# Revit family: Hager-GOLF-Flush_mounted-IP40-With_Cover-With_DIN-NoHosted-PL-pl
name_source: partatom
category: Electrical Equipment
units: mm (PartAtom-declared; Revit-internal decimal feet)

## family parameters
Always vertical = Yes
Cut with Voids When Loaded = No
Maintain Annotation Orientation = No
Panel Configuration = Two Columns, Circuits Across
Part Type = Panelboard
Room Calculation Point = No
Round Connector Dimension = Use Diameter
Shared = No
Work Plane-Based = Yes

## types (25) — shared parameters
Code hager = ADD-EC000214_EU
Default Elevation = 1200 mm
EF000003 - Sposób montażu = Montaż podtynkowy
EF000007 - Kolor = Biały
EF000024 - Odporność na promieniowanie UV = No
EF000049 - Głębokość = 97 mm  [stored 0.318241 ft]
EF000116 - Numer RAL = 9010
EF000218 - Głębokość wbudowania = 72 mm  [stored 0.23622 ft]
EF001062 - Wykonanie zgodne z Dyrektywą Kompatybilności Elektromagnetycznej EMC = No
EF001088 - Możliwość rozbudowy = Yes
EF001134 - Szyna DIN = Yes
EF004462 - Rodzaj zamknięcia = Inne
EF005474 - Stopień ochrony (IP) = IP40
EF006306 - Z zamkiem = No
EF015941 - Drzwi przepuszczające sygnał = Yes
ETIM class code = EC000214
ETIM class name = Small distribution board
HG000001-Number of columns-pl = 1
HG000002-with door or cover-pl = Yes
HG000003-Range-pl = GOLF
HG000005-Thickness-pl = 2 mm  [stored 0.00656168 ft]
HG000006-Flush mounted-pl = Yes
HG000009-Double swing door-pl = No
HG000010-Asymmetric doors-pl = No
HG000011-Empty rows from bottom-pl = No
HG000012-Door swing angle-pl = 90.00°
HG000013-Door on the left-pl = No
HG000014-Door on the right-pl = Yes
HG000015-Clearance visibility-pl = Yes
HG000016-Door 3D visibility-pl = Yes
HG000017-Distance between poles-pl = 18 mm  [stored 0.0590551 ft]
HG000060-RAL-number = 9010
HG000099-Onfly Template ID-pl-PL = 507532
Manufacturer = Hager
Name BIM&CO = Electricity
Name hager = ADD_Enclosures_EC000214
Reference = Template-Enclosure_EU-EC000214
Uniformat = Low Tension Service & Dist.
Uniformat code = D501001
zero-valued in all types: EF001131 - Głębokość wewnętrzna, HG000007-Number of empty columns-pl, HG000008-Number of empty rows-pl

## per-type parameters (varying)
| type | BC_METADATA | EF000008 - Szerokość | EF000040 - Wysokość | EF000118 - Z płytą montażową | EF000266 - Liczba rzędów | EF000332 - Wysokość wbudowania | EF000846 - Szerokość wbudowania | EF002950 - Szerokość wyrażona liczbą modułów | EF006244 - Transparentna pokrywa/drzwi | EF009212 - Wykonanie/rodzaj pokrywy | EF015776 - Listwa zaciskowa uziemienia | EF015777 - Listwa zaciskowa przewodu neutralnego | HG000004-Manufacturer reference-pl | HGEF000266-Liczba rzędów | HGEF0002950-Szerokość wyrażona liczbą modułów |
| GOLF-Flush_mounted_W204_H225_D97_4_Modular_Spacing-VF104PD | {"ObjectGuid":"4110ddcc-8f0d-44ed-8822-63e9be82c284","ModelGuid":"366267af-4815-4317-b628-b26145f090ec","VariantGuid":"5908c0a0-e7f0-400e-9d29-8d09325588ac","Revision":"#12","VariantName":"GOLF-Flush_mounted_W204_H225_D97_4_Modular_Spacing-VF104PD"} | 204 mm | 225 mm  [stored 0.738189 ft] | No | 1 | 189 mm  [stored 0.620079 ft] | 170 mm  [stored 0.557743 ft] | 4 | No | Zamknięty | Yes | Yes | VF104PD | 1 | 4 |
| GOLF-Flush_mounted_W204_H225_D97_4_Modular_Spacing-VF104TD | {"ObjectGuid":"4110ddcc-8f0d-44ed-8822-63e9be82c284","ModelGuid":"366267af-4815-4317-b628-b26145f090ec","VariantGuid":"e0216446-62ca-4817-b7ef-b2e9ca912061","Revision":"#12","VariantName":"GOLF-Flush_mounted_W204_H225_D97_4_Modular_Spacing-VF104TD"} | 204 mm | 225 mm  [stored 0.738189 ft] | No | 1 | 189 mm  [stored 0.620079 ft] | 170 mm  [stored 0.557743 ft] | 4 | Yes | Zamknięty | Yes | Yes | VF104TD | 1 | 4 |
| GOLF-Flush_mounted_W275_H225_D97_8_Modular_Spacing-VF108PD | {"ObjectGuid":"4110ddcc-8f0d-44ed-8822-63e9be82c284","ModelGuid":"366267af-4815-4317-b628-b26145f090ec","VariantGuid":"b03ebf87-6662-491a-b6a8-509a16b323ed","Revision":"#12","VariantName":"GOLF-Flush_mounted_W275_H225_D97_8_Modular_Spacing-VF108PD"} | 275 mm | 225 mm  [stored 0.738189 ft] | No | 1 | 189 mm  [stored 0.620079 ft] | 242 mm  [stored 0.793963 ft] | 8 | No | Zamknięty | Yes | Yes | VF108PD | 1 | 8 |
| GOLF-Flush_mounted_W275_H225_D97_8_Modular_Spacing-VF108TD | {"ObjectGuid":"4110ddcc-8f0d-44ed-8822-63e9be82c284","ModelGuid":"366267af-4815-4317-b628-b26145f090ec","VariantGuid":"675cc267-a1fb-44dc-9656-e9b862e703bb","Revision":"#12","VariantName":"GOLF-Flush_mounted_W275_H225_D97_8_Modular_Spacing-VF108TD"} | 275 mm | 225 mm  [stored 0.738189 ft] | No | 1 | 189 mm  [stored 0.620079 ft] | 242 mm  [stored 0.793963 ft] | 8 | Yes | Zamknięty | Yes | Yes | VF108TD | 1 | 8 |
| GOLF-Flush_mounted_W352_H293_D97_12_Modular_Spacing-VF112PD | {"ObjectGuid":"4110ddcc-8f0d-44ed-8822-63e9be82c284","ModelGuid":"366267af-4815-4317-b628-b26145f090ec","VariantGuid":"7fc8be5a-4e42-4c11-bf83-f1857e61b970","Revision":"#12","VariantName":"GOLF-Flush_mounted_W352_H293_D97_12_Modular_Spacing-VF112PD"} | 352 mm  [stored 1.15486 ft] | 293 mm | No | 1 | 257 mm  [stored 0.843176 ft] | 318 mm  [stored 1.04331 ft] | 12 | No | Zamknięty | Yes | Yes | VF112PD | 1 | 12 |
| GOLF-Flush_mounted_W352_H293_D97_12_Modular_Spacing-VF112TD | {"ObjectGuid":"4110ddcc-8f0d-44ed-8822-63e9be82c284","ModelGuid":"366267af-4815-4317-b628-b26145f090ec","VariantGuid":"7087be8a-5bcc-4a63-bb2f-b231d84baee1","Revision":"#12","VariantName":"GOLF-Flush_mounted_W352_H293_D97_12_Modular_Spacing-VF112TD"} | 352 mm  [stored 1.15486 ft] | 293 mm | No | 1 | 257 mm  [stored 0.843176 ft] | 318 mm  [stored 1.04331 ft] | 12 | Yes | Zamknięty | Yes | Yes | VF112TD | 1 | 12 |
| GOLF-Flush_mounted_W460_H293_D97_18_Modular_Spacing-VF118PD | {"ObjectGuid":"4110ddcc-8f0d-44ed-8822-63e9be82c284","ModelGuid":"366267af-4815-4317-b628-b26145f090ec","VariantGuid":"b158a517-640d-4d6e-841f-1372ac4b0368","Revision":"#12","VariantName":"GOLF-Flush_mounted_W460_H293_D97_18_Modular_Spacing-VF118PD"} | 460 mm  [stored 1.50919 ft] | 293 mm | No | 1 | 257 mm  [stored 0.843176 ft] | 426 mm  [stored 1.39764 ft] | 18 | No | Zamknięty | Yes | Yes | VF118PD | 1 | 18 |
| GOLF-Flush_mounted_W460_H293_D97_18_Modular_Spacing-VF118TD | {"ObjectGuid":"4110ddcc-8f0d-44ed-8822-63e9be82c284","ModelGuid":"366267af-4815-4317-b628-b26145f090ec","VariantGuid":"ca84ee14-7eb6-47c0-83a6-df2615128fcd","Revision":"#12","VariantName":"GOLF-Flush_mounted_W460_H293_D97_18_Modular_Spacing-VF118TD"} | 460 mm  [stored 1.50919 ft] | 293 mm | No | 1 | 257 mm  [stored 0.843176 ft] | 426 mm  [stored 1.39764 ft] | 18 | Yes | Zamknięty | Yes | Yes | VF118TD | 1 | 18 |
| GOLF-Flush_mounted_W532_H293_D97_22_Modular_Spacing-VF122PD | {"ObjectGuid":"4110ddcc-8f0d-44ed-8822-63e9be82c284","ModelGuid":"366267af-4815-4317-b628-b26145f090ec","VariantGuid":"20600b5c-545e-4896-ae9a-10930eba1918","Revision":"#12","VariantName":"GOLF-Flush_mounted_W532_H293_D97_22_Modular_Spacing-VF122PD"} | 532 mm  [stored 1.74541 ft] | 293 mm | No | 1 | 257 mm  [stored 0.843176 ft] | 498 mm  [stored 1.63386 ft] | 22 | No | Zamknięty | Yes | Yes | VF122PD | 1 | 22 |
| GOLF-Flush_mounted_W532_H293_D97_22_Modular_Spacing-VF122TD | {"ObjectGuid":"4110ddcc-8f0d-44ed-8822-63e9be82c284","ModelGuid":"366267af-4815-4317-b628-b26145f090ec","VariantGuid":"3ea3431d-0f5a-43d9-ab3e-3197dd213b15","Revision":"#12","VariantName":"GOLF-Flush_mounted_W532_H293_D97_22_Modular_Spacing-VF122TD"} | 532 mm  [stored 1.74541 ft] | 293 mm | No | 1 | 257 mm  [stored 0.843176 ft] | 498 mm  [stored 1.63386 ft] | 22 | Yes | Zamknięty | Yes | Yes | VF122TD | 1 | 22 |
| GOLF-Flush_mounted_W382_H418_D97_12_Modular_Spacing-VF212PD | {"ObjectGuid":"4110ddcc-8f0d-44ed-8822-63e9be82c284","ModelGuid":"366267af-4815-4317-b628-b26145f090ec","VariantGuid":"c9d7dccc-fa58-4548-96f4-ed19e04cd73f","Revision":"#12","VariantName":"GOLF-Flush_mounted_W382_H418_D97_12_Modular_Spacing-VF212PD"} | 382 mm  [stored 1.25328 ft] | 418 mm  [stored 1.37139 ft] | No | 2 | 382 mm  [stored 1.25328 ft] | 318 mm  [stored 1.04331 ft] | 12 | No | Zamknięty | Yes | Yes | VF212PD | 2 | 12 |
| GOLF-Flush_mounted_W382_H418_D97_12_Modular_Spacing-VF212TD | {"ObjectGuid":"4110ddcc-8f0d-44ed-8822-63e9be82c284","ModelGuid":"366267af-4815-4317-b628-b26145f090ec","VariantGuid":"3d59abc7-9114-4b17-869a-c3cebf26ed1e","Revision":"#12","VariantName":"GOLF-Flush_mounted_W382_H418_D97_12_Modular_Spacing-VF212TD"} | 382 mm  [stored 1.25328 ft] | 418 mm  [stored 1.37139 ft] | No | 2 | 382 mm  [stored 1.25328 ft] | 318 mm  [stored 1.04331 ft] | 12 | Yes | Zamknięty | Yes | Yes | VF212TD | 2 | 12 |
| GOLF-Flush_mounted_W460_H418_D97_18_Modular_Spacing-VF218PD | {"ObjectGuid":"4110ddcc-8f0d-44ed-8822-63e9be82c284","ModelGuid":"366267af-4815-4317-b628-b26145f090ec","VariantGuid":"1d6ba3ca-fa95-485b-8160-6e344684a26f","Revision":"#12","VariantName":"GOLF-Flush_mounted_W460_H418_D97_18_Modular_Spacing-VF218PD"} | 460 mm  [stored 1.50919 ft] | 418 mm  [stored 1.37139 ft] | No | 2 | 382 mm  [stored 1.25328 ft] | 426 mm  [stored 1.39764 ft] | 18 | No | Zamknięty | Yes | Yes | VF218PD | 2 | 18 |
| GOLF-Flush_mounted_W460_H418_D97_18_Modular_Spacing-VF218PZF | {"ObjectGuid":"4110ddcc-8f0d-44ed-8822-63e9be82c284","ModelGuid":"366267af-4815-4317-b628-b26145f090ec","VariantGuid":"cb853cd3-43c5-45b2-8cc4-e8834975f61a","Revision":"#12","VariantName":"GOLF-Flush_mounted_W460_H418_D97_18_Modular_Spacing-VF218PZF"} | 460 mm  [stored 1.50919 ft] | 418 mm  [stored 1.37139 ft] | Yes | 2 | 375 mm  [stored 1.23031 ft] | 426 mm  [stored 1.39764 ft] | 18 | No | Z otworem | No | No | VF218PZF | 2 | 18 |
| GOLF-Flush_mounted_W460_H418_D97_18_Modular_Spacing-VF218TD | {"ObjectGuid":"4110ddcc-8f0d-44ed-8822-63e9be82c284","ModelGuid":"366267af-4815-4317-b628-b26145f090ec","VariantGuid":"1f9e89e2-d819-45e6-914e-b4308898904e","Revision":"#12","VariantName":"GOLF-Flush_mounted_W460_H418_D97_18_Modular_Spacing-VF218TD"} | 460 mm  [stored 1.50919 ft] | 418 mm  [stored 1.37139 ft] | No | 2 | 382 mm  [stored 1.25328 ft] | 426 mm  [stored 1.39764 ft] | 18 | Yes | Zamknięty | Yes | Yes | VF218TD | 2 | 18 |
| GOLF-Flush_mounted_W352_H543_D97_12_Modular_Spacing-VF312PD | {"ObjectGuid":"4110ddcc-8f0d-44ed-8822-63e9be82c284","ModelGuid":"366267af-4815-4317-b628-b26145f090ec","VariantGuid":"bed8d0b2-0b0f-4205-956a-704c5ed13bc4","Revision":"#12","VariantName":"GOLF-Flush_mounted_W352_H543_D97_12_Modular_Spacing-VF312PD"} | 352 mm  [stored 1.15486 ft] | 543 mm  [stored 1.7815 ft] | No | 3 | 507 mm  [stored 1.66339 ft] | 318 mm  [stored 1.04331 ft] | 12 | No | Zamknięty | Yes | Yes | VF312PD | 3 | 12 |
| GOLF-Flush_mounted_W352_H543_D97_12_Modular_Spacing-VF312TD | {"ObjectGuid":"4110ddcc-8f0d-44ed-8822-63e9be82c284","ModelGuid":"366267af-4815-4317-b628-b26145f090ec","VariantGuid":"4611a291-4d16-41a3-bf6f-a9690ae8496e","Revision":"#12","VariantName":"GOLF-Flush_mounted_W352_H543_D97_12_Modular_Spacing-VF312TD"} | 352 mm  [stored 1.15486 ft] | 543 mm  [stored 1.7815 ft] | No | 3 | 507 mm  [stored 1.66339 ft] | 318 mm  [stored 1.04331 ft] | 12 | Yes | Zamknięty | Yes | Yes | VF312TD | 3 | 12 |
| GOLF-Flush_mounted_W460_H543_D97_18_Modular_Spacing-VF318PD | {"ObjectGuid":"4110ddcc-8f0d-44ed-8822-63e9be82c284","ModelGuid":"366267af-4815-4317-b628-b26145f090ec","VariantGuid":"4f0ec00a-b5a9-4147-be91-f01800621063","Revision":"#12","VariantName":"GOLF-Flush_mounted_W460_H543_D97_18_Modular_Spacing-VF318PD"} | 460 mm  [stored 1.50919 ft] | 543 mm  [stored 1.7815 ft] | No | 3 | 507 mm  [stored 1.66339 ft] | 426 mm  [stored 1.39764 ft] | 18 | No | Zamknięty | Yes | Yes | VF318PD | 3 | 18 |
| GOLF-Flush_mounted_W460_H543_D97_18_Modular_Spacing-VF318PZF | {"ObjectGuid":"4110ddcc-8f0d-44ed-8822-63e9be82c284","ModelGuid":"366267af-4815-4317-b628-b26145f090ec","VariantGuid":"ffe10ad1-ec7d-4383-b245-dc8b3c33b52d","Revision":"#12","VariantName":"GOLF-Flush_mounted_W460_H543_D97_18_Modular_Spacing-VF318PZF"} | 460 mm  [stored 1.50919 ft] | 543 mm  [stored 1.7815 ft] | Yes | 3 | 495 mm  [stored 1.62402 ft] | 426 mm  [stored 1.39764 ft] | 18 | No | Z otworem | No | No | VF318PZF | 3 | 18 |
| GOLF-Flush_mounted_W460_H543_D97_18_Modular_Spacing-VF318TD | {"ObjectGuid":"4110ddcc-8f0d-44ed-8822-63e9be82c284","ModelGuid":"366267af-4815-4317-b628-b26145f090ec","VariantGuid":"86e31d80-f2d9-4224-b379-21d39aac99c4","Revision":"#12","VariantName":"GOLF-Flush_mounted_W460_H543_D97_18_Modular_Spacing-VF318TD"} | 460 mm  [stored 1.50919 ft] | 543 mm  [stored 1.7815 ft] | No | 3 | 507 mm  [stored 1.66339 ft] | 426 mm  [stored 1.39764 ft] | 18 | Yes | Zamknięty | Yes | Yes | VF318TD | 3 | 18 |
| GOLF-Flush_mounted_W352_H688_D97_12_Modular_Spacing-VF412PD | {"ObjectGuid":"4110ddcc-8f0d-44ed-8822-63e9be82c284","ModelGuid":"366267af-4815-4317-b628-b26145f090ec","VariantGuid":"ec0cadac-24a4-4d01-8346-892c24aca867","Revision":"#12","VariantName":"GOLF-Flush_mounted_W352_H688_D97_12_Modular_Spacing-VF412PD"} | 352 mm  [stored 1.15486 ft] | 688 mm  [stored 2.25722 ft] | No | 4 | 652 mm  [stored 2.13911 ft] | 318 mm  [stored 1.04331 ft] | 12 | No | Zamknięty | Yes | Yes | VF412PD | 4 | 12 |
| GOLF-Flush_mounted_W352_H688_D97_12_Modular_Spacing-VF412TD | {"ObjectGuid":"4110ddcc-8f0d-44ed-8822-63e9be82c284","ModelGuid":"366267af-4815-4317-b628-b26145f090ec","VariantGuid":"e149fd93-a0fa-4f68-aa2b-6c3095a2ce4e","Revision":"#12","VariantName":"GOLF-Flush_mounted_W352_H688_D97_12_Modular_Spacing-VF412TD"} | 352 mm  [stored 1.15486 ft] | 688 mm  [stored 2.25722 ft] | No | 4 | 652 mm  [stored 2.13911 ft] | 318 mm  [stored 1.04331 ft] | 12 | Yes | Zamknięty | Yes | Yes | VF412TD | 4 | 12 |
| GOLF-Flush_mounted_W460_H688_D97_18_Modular_Spacing-VF418PD | {"ObjectGuid":"4110ddcc-8f0d-44ed-8822-63e9be82c284","ModelGuid":"366267af-4815-4317-b628-b26145f090ec","VariantGuid":"e8d7b7df-78f6-4d06-bd81-82726216d978","Revision":"#12","VariantName":"GOLF-Flush_mounted_W460_H688_D97_18_Modular_Spacing-VF418PD"} | 460 mm  [stored 1.50919 ft] | 688 mm  [stored 2.25722 ft] | No | 4 | 652 mm  [stored 2.13911 ft] | 426 mm  [stored 1.39764 ft] | 18 | No | Zamknięty | Yes | Yes | VF418PD | 4 | 18 |
| GOLF-Flush_mounted_W460_H688_D97_18_Modular_Spacing-VF418PZF | {"ObjectGuid":"4110ddcc-8f0d-44ed-8822-63e9be82c284","ModelGuid":"366267af-4815-4317-b628-b26145f090ec","VariantGuid":"b8084d96-c0ca-4bc0-882a-f335ffbef05f","Revision":"#12","VariantName":"GOLF-Flush_mounted_W460_H688_D97_18_Modular_Spacing-VF418PZF"} | 460 mm  [stored 1.50919 ft] | 688 mm  [stored 2.25722 ft] | Yes | 4 | 640 mm  [stored 2.09974 ft] | 426 mm  [stored 1.39764 ft] | 18 | No | Z otworem | No | No | VF418PZF | 4 | 18 |
| GOLF-Flush_mounted_W460_H688_D97_18_Modular_Spacing-VF418TD | {"ObjectGuid":"4110ddcc-8f0d-44ed-8822-63e9be82c284","ModelGuid":"366267af-4815-4317-b628-b26145f090ec","VariantGuid":"06af79f9-2e4b-4ef4-92ee-6dc80e1cd18e","Revision":"#12","VariantName":"GOLF-Flush_mounted_W460_H688_D97_18_Modular_Spacing-VF418TD"} | 460 mm  [stored 1.50919 ft] | 688 mm  [stored 2.25722 ft] | No | 4 | 652 mm  [stored 2.13911 ft] | 426 mm  [stored 1.39764 ft] | 18 | Yes | Zamknięty | Yes | Yes | VF418TD | 4 | 18 |

note: [stored X ft] marks values corroborated as IEEE doubles in the binary element streams (Revit-internal decimal feet)

## geometry (parser evidence)
native form markers: Sweep x15
no freeform markers — native parametric forms only
